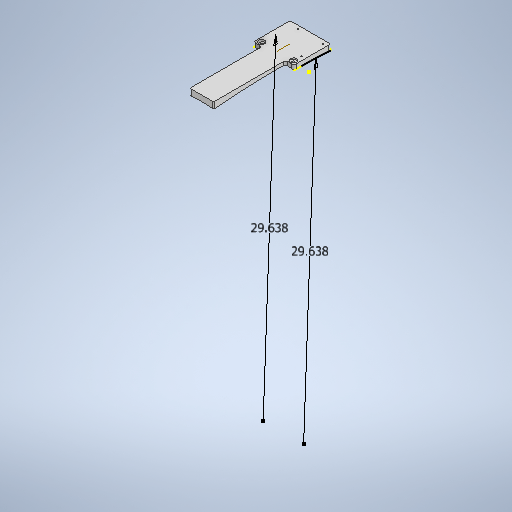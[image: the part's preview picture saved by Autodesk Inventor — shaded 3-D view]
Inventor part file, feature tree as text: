
AUTODESK INVENTOR PART (.ipt)
format: ipt  version: 2025 (Build 290162000, 162)  size: 571,904 bytes
history: native  units: in
note: dims shown in document units (in); Inventor stores cm internally (conversion verified against a paired STEP export)
features: sketch x15, extrude x10, other x4, mirror x2, loft x2, fillet x2, revolve x1, plane x1
ambient origin geometry x8: Origin, YZ Plane, XZ Plane, XY Plane, X Axis, Y Axis, Z Axis, Center Point
bodies: Solid1 (feature_tree)
feature tree (37):
  extrude  "Extrusion1"  Depth=1.5in
  revolve  "Revolution1"  [1 undecoded]
  extrude  "Extrusion2"  Depth=0.0563in
  plane  "Work Plane9"
  mirror  "Mirror1"
  extrude  "Extrusion3"  TaperAngle=90.0deg  [1 undecoded]
  mirror  "Mirror2"
  extrude  "Extrusion4"  TaperAngle=90.0deg  [1 undecoded]
  extrude  "Extrusion5"  Depth=0.6748in
  extrude  "Extrusion8"  TaperAngle=180.0deg  [1 undecoded]
  sketch  "Sketch10"  dims[d17=1.0in d18=0.0in d27=-1.8228in]
  sketch  "Sketch11"  dims[d28=1.0in d29=0.0in d30=0.356in]
  sketch  "Sketch12"  dims[d31=90.0deg d32=0.712in]
  loft  "Loft2"
  extrude  "Extrusion9"  Depth=0.356in
  extrude  "Extrusion10"  Depth=0.712in
  extrude  "Extrusion11"  Depth=2.585in
  loft  "Loft3"
  fillet  "Fillet2"  Radius=0.33in
  fillet  "Fillet3"  Radius=0.11in
  extrude  "Extrusion12"  Depth=1.93in
  sketch  "Sketch1"  dims[d2=0.25in d3=1.5in]
  sketch  "Sketch2"  dims[d4=1.0in d5=0.0in d6=0.1in]
  sketch  "Sketch3"  dims[d7=0.12in d8=0.0563in]
  sketch  "Sketch5"  dims[d9=0.2in d10=90.0deg]
  sketch  "Sketch6"  dims[d11=0.275in d12=90.0deg]
  sketch  "Sketch7"  dims[d13=0.15in d14=0.6748in]
  sketch  "Sketch8"  dims[d15=0.1in d16=180.0deg]
  other  "Edges3"
  other  "Edges4"
  sketch  "Sketch13"  dims[d33=1.0in d34=0.0in d52=2.585in]
  sketch  "Sketch14"  dims[d53=2.585in d54=0.36in d55=0.33in d56=0.11in]
  sketch  "Sketch15"  dims[d57=2.27in d58=1.93in]
  sketch  "Sketch16"  dims[d59=0.11in]
  other  "Edges5"
  other  "Edges6"
  sketch  "Sketch17"  dims[d60=0.11in d61=0.11in d62=0.2in d63=0.0in d64=0.345in d65=0.099in d66=0.099in d76=0.11in d77=0.001in d78=0.0in d79=29.638in d80=29.638in d81=0.0in d82=90.0deg d83=0.0in d84=90.0deg d85=0.0in d86=90.0deg d87=6.5in d88=1.07in d89=2.14in d90=0.1in d91=0.0in d92=0.51in d93=0.075in d94=0.075in d95=0.001in d96=0.0in d97=0.001in d98=0.0in d99=0.0in d100=90.0deg d101=0.0in d102=90.0deg d103=0.0in d104=90.0deg d105=0.125in d106=0.2in d107=0.113in d108=0.113in d109=0.113in d110=0.113in d111=2.0in d112=0.0in]
note: 4 required parameter values undecoded (feature->parameter linkage not recoverable at this tier; creation-order binding heuristic only, values carry confidence <= 0.55)